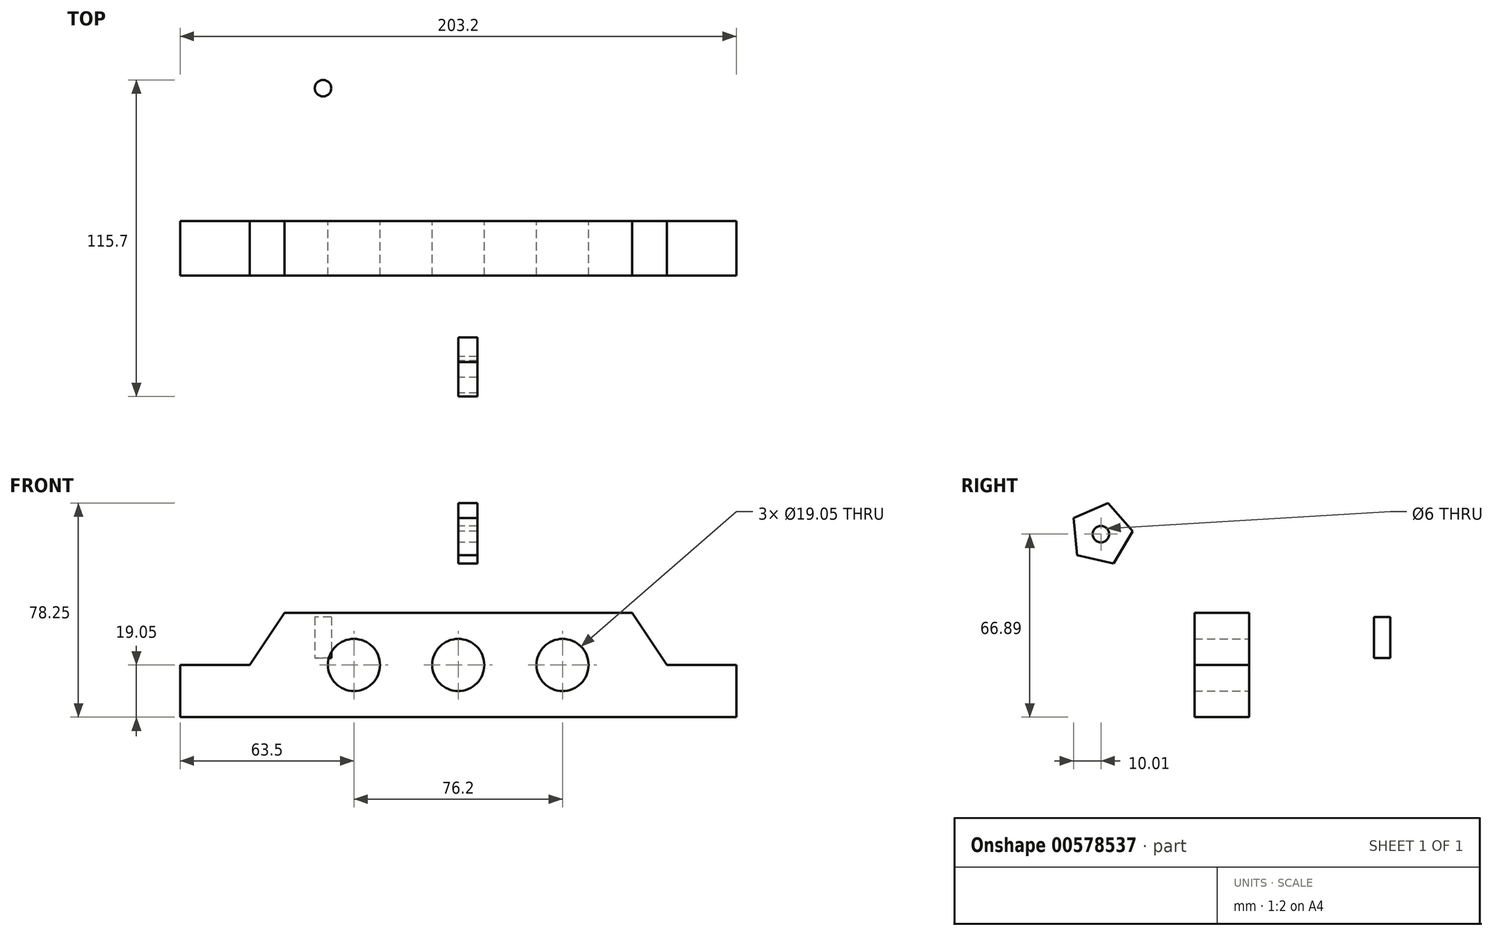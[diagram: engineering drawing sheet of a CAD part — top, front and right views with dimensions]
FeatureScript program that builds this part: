
annotation { "Feature Type Name" : "Feature", "Feature Type Description" : "" }
export const myFeature = defineFeature(function(context is Context, id is Id, definition is map)
    precondition{}
    {
        {
            var Q0;
            Q0=qCreatedBy(makeId("Front.planeOp"),FACE);
            var sketch = newSketch(context, id + "F0", { "sketchPlane" : qUnion([Q0])});
            skLineSegment(sketch, "E0.bottom", {"start": v(-63.5, 16.5) * mm, "end": v(63.5, 16.5) * mm});
            skLineSegment(sketch, "E0.top", {"start": v(-101.6, -21.59) * mm, "end": v(101.6, -21.59) * mm});
            skLineSegment(sketch, "E0.left", {"start": v(-101.6, -2.54) * mm, "end": v(-101.6, -21.59) * mm});
            skLineSegment(sketch, "E0.right", {"start": v(101.6, -2.54) * mm, "end": v(101.6, -21.59) * mm});
            skLineSegment(sketch, "E1", {"start": v(-101.6, -2.54) * mm, "end": v(-76.2, -2.54) * mm});
            skLineSegment(sketch, "E2", {"start": v(-76.2, -2.54) * mm, "end": v(-63.5, 16.51) * mm});
            skCircle(sketch, "E3", {"center": v(-38.1, -2.54) * mm, "radius": 9.53 * mm});
            skCircle(sketch, "E4", {"center": v(0, -2.54) * mm, "radius": 9.53 * mm});
            skPoint(sketch, "E5.orphan", {"position": v(-101.6, 16.5) * mm});
            skLineSegment(sketch, "E6.MirrorCS", {"start": v(76.2, -2.54) * mm, "end": v(63.5, 16.51) * mm});
            skLineSegment(sketch, "E7.MirrorCS", {"start": v(101.6, -2.54) * mm, "end": v(76.2, -2.54) * mm});
            skPoint(sketch, "E8.orphan", {"position": v(101.6, 16.5) * mm});
            skCircle(sketch, "E9.MirrorC", {"center": v(38.1, -2.54) * mm, "radius": 9.53 * mm});
            skPoint(sketch, "E10.orphan", {"position": v(0, 16.5) * mm});
            skPoint(sketch, "E11.orphan", {"position": v(0, -21.59) * mm});
            skSolve(sketch);
        }
        {
            var Q0;
            Q0=makeQuery(id+"F0.imprint","IMPRINT",FACE,{"disambiguationData":[TD([[makeQuery(id+"F0.imprint","IMPRINT",EDGE,{"derivedFrom":sQuery(id+"F0.wireOp",EDGE,"E0.bottom")}),-1.0]])]});
            extrude(context, id + "F1", {"entities" : qUnion([Q0]), "depth" : 20 * mm, "offsetDistance" : 25 * mm});
        }
        {
            var Q0;
            Q0=qCreatedBy(makeId("Top.planeOp"),FACE);
            var sketch = newSketch(context, id + "F2", { "sketchPlane" : qUnion([Q0])});
            skCircle(sketch, "E12", {"center": v(-49.39, 48.54) * mm, "radius": 3 * mm});
            skSolve(sketch);
        }
        {
            var Q0;
            Q0=makeQuery(id+"F2.imprint","IMPRINT",FACE,{"disambiguationData":[TD([[makeQuery(id+"F2.imprint","IMPRINT",EDGE,{"derivedFrom":sQuery(id+"F2.wireOp",EDGE,"E12")}),1.0]])]});
            extrude(context, id + "F3", {"entities" : qUnion([Q0]), "depth" : 15 * mm, "offsetDistance" : 25 * mm});
        }
        {
            var Q0;
            Q0=qCreatedBy(makeId("Right.planeOp"),FACE);
            var sketch = newSketch(context, id + "F4", { "sketchPlane" : qUnion([Q0])});
            skCircle(sketch, "E13.cCircle", {"center": v(-54.15, 45.3) * mm, "radius": 9.42 * mm, "construction": true});
            skLineSegment(sketch, "E13.0", {"start": v(-42.56, 46.39) * mm, "end": v(-49.54, 34.62) * mm});
            skLineSegment(sketch, "E13.1", {"start": v(-49.54, 34.62) * mm, "end": v(-62.89, 37.61) * mm});
            skLineSegment(sketch, "E13.2", {"start": v(-62.89, 37.61) * mm, "end": v(-64.16, 51.23) * mm});
            skLineSegment(sketch, "E13.3", {"start": v(-64.16, 51.23) * mm, "end": v(-51.6, 56.66) * mm});
            skLineSegment(sketch, "E13.4", {"start": v(-51.6, 56.66) * mm, "end": v(-42.56, 46.39) * mm});
            skPoint(sketch, "E13.0.midPoint", {"position": v(-46.05, 40.5) * mm});
            skSolve(sketch);
        }
        {
            var Q0;
            Q0 = qSketchRegion(id + "F4", true);
            extrude(context, id + "F5", {"entities" : qUnion([Q0]), "depth" : 7 * mm, "offsetDistance" : 25 * mm});
        }
        {
            var Q0;
            Q0=makeQuery(id+"F5.opExtrude","CAP_FACE",FACE,{"disambiguationData":[OSD([sQuery(id+"F4.wireOp",EDGE,"E13.0"),sQuery(id+"F4.wireOp",EDGE,"E13.1"),sQuery(id+"F4.wireOp",EDGE,"E13.2"),sQuery(id+"F4.wireOp",EDGE,"E13.3"),sQuery(id+"F4.wireOp",EDGE,"E13.4")])],"isStart":true});
            var sketch = newSketch(context, id + "F6", { "sketchPlane" : qUnion([Q0])});
            skCircle(sketch, "E14", {"center": v(54.15, 45.3) * mm, "radius": 11.64 * mm});
            skSolve(sketch);
        }
        {
            var Q0;
            Q0=sQuery(id+"F6.wireOp",VERTEX,"E14.center");
            var Q1;
            Q1=makeQuery(id+"F5.opExtrude","SWEPT_BODY",BODY,{"disambiguationData":[OSD([sQuery(id+"F4.wireOp",EDGE,"E13.0"),sQuery(id+"F4.wireOp",EDGE,"E13.1"),sQuery(id+"F4.wireOp",EDGE,"E13.2"),sQuery(id+"F4.wireOp",EDGE,"E13.3"),sQuery(id+"F4.wireOp",EDGE,"E13.4")])]});
            hole(context, id + "F7", {"style" : HoleStyle.SIMPLE, "endStyle" : HoleEndStyle.THROUGH, "holeDiameter" : 6 * mm, "majorDiameter" : 5 * mm, "isTappedThrough" : true, "tappedDepth" : 12 * mm, "tapClearance" : 3, "locations" : qUnion([Q0]), "scope" : qUnion([Q1])});
        }
    });
